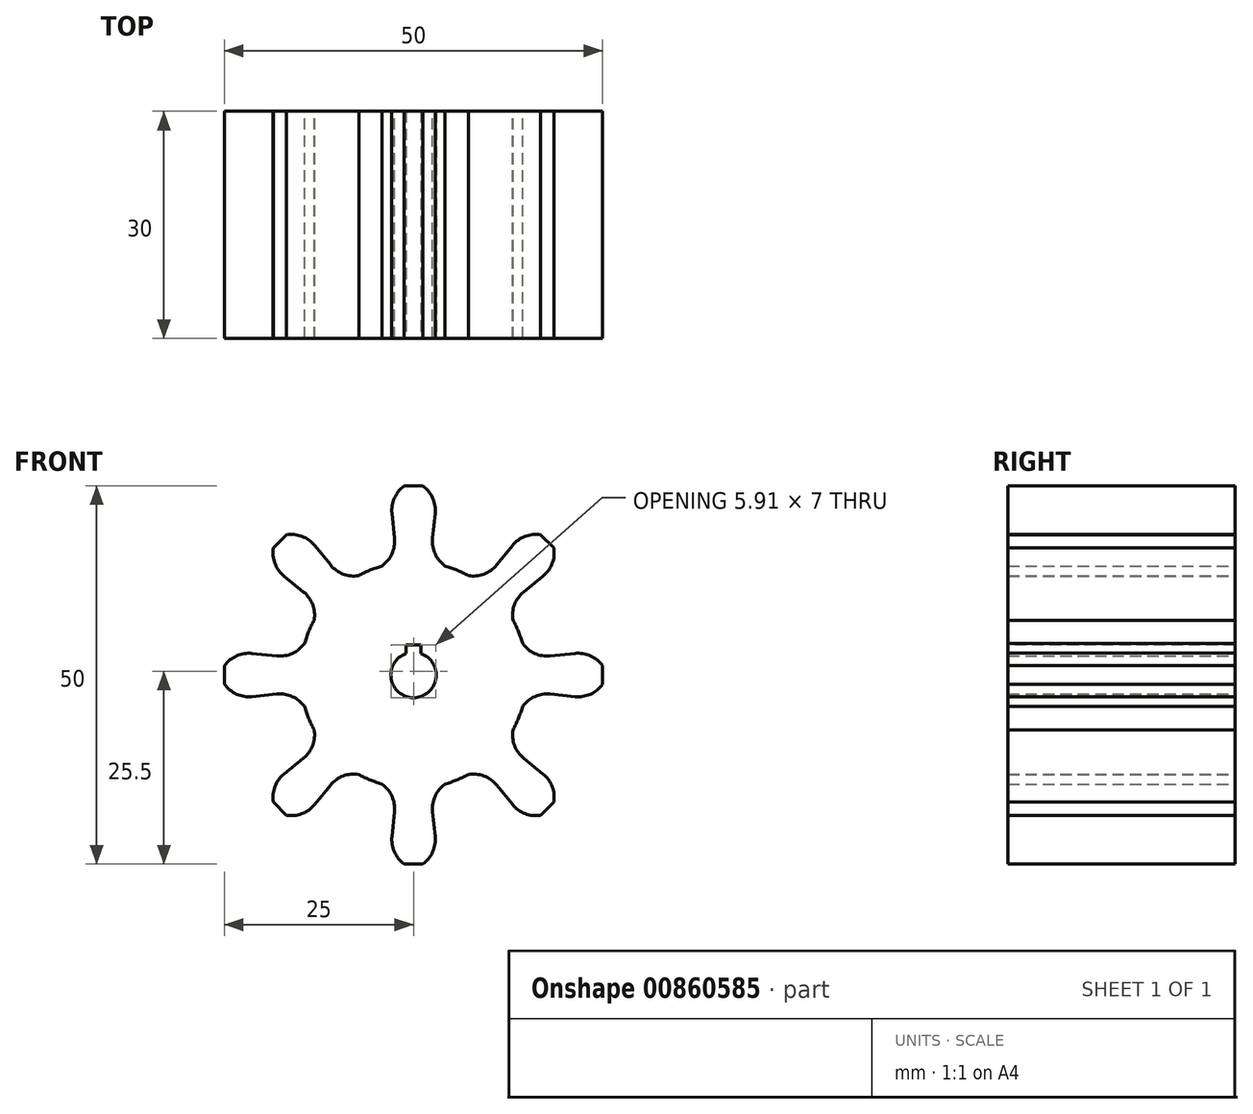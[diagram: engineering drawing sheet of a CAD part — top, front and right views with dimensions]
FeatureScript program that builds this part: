
annotation { "Feature Type Name" : "Feature", "Feature Type Description" : "" }
export const myFeature = defineFeature(function(context is Context, id is Id, definition is map)
    precondition{}
    {
        {
            var Q0;
            Q0=qCreatedBy(makeId("Front.planeOp"),FACE);
            var sketch = newSketch(context, id + "F0", { "sketchPlane" : qUnion([Q0])});
            skArc(sketch, "E0", {"start": v(-13.14, 7.24) * mm, "mid": v(-13.86, 5.74) * mm, "end": v(-14.4, 4.17) * mm});
            skArc(sketch, "E1", {"start": v(-4.17, 14.4) * mm, "mid": v(-2.86, 16.01) * mm, "end": v(-2.53, 18.06) * mm});
            skLineSegment(sketch, "E2", {"start": v(-2.53, 18.06) * mm, "end": v(-2.86, 21.35) * mm});
            skLineSegment(sketch, "E3", {"start": v(-1.22, 25) * mm, "end": v(1.22, 25) * mm});
            skArc(sketch, "E4", {"start": v(-1.22, 25) * mm, "mid": v(-2.53, 23.4) * mm, "end": v(-2.86, 21.35) * mm});
            skArc(sketch, "E5.MirrorCS", {"start": v(1.22, 25) * mm, "mid": v(2.53, 23.4) * mm, "end": v(2.86, 21.35) * mm});
            skLineSegment(sketch, "E6.MirrorCS", {"start": v(2.53, 18.06) * mm, "end": v(2.86, 21.35) * mm});
            skArc(sketch, "E7.MirrorCS", {"start": v(4.17, 14.4) * mm, "mid": v(2.86, 16.01) * mm, "end": v(2.53, 18.06) * mm});
            skLineSegment(sketch, "E8.1.0", {"start": v(-18.54, 16.81) * mm, "end": v(-16.81, 18.54) * mm});
            skArc(sketch, "E8.1.1", {"start": v(-18.54, 16.81) * mm, "mid": v(-18.33, 14.75) * mm, "end": v(-17.12, 13.07) * mm});
            skLineSegment(sketch, "E8.1.2", {"start": v(-14.56, 10.98) * mm, "end": v(-17.12, 13.07) * mm});
            skArc(sketch, "E8.1.3", {"start": v(-13.14, 7.24) * mm, "mid": v(-13.34, 9.3) * mm, "end": v(-14.56, 10.98) * mm});
            skArc(sketch, "E8.1.4", {"start": v(-7.24, 13.14) * mm, "mid": v(-9.3, 13.34) * mm, "end": v(-10.98, 14.56) * mm});
            skLineSegment(sketch, "E8.1.5", {"start": v(-10.98, 14.56) * mm, "end": v(-13.07, 17.12) * mm});
            skArc(sketch, "E8.1.6", {"start": v(-16.81, 18.54) * mm, "mid": v(-14.75, 18.33) * mm, "end": v(-13.07, 17.12) * mm});
            skLineSegment(sketch, "E8.2.0", {"start": v(-25, -1.22) * mm, "end": v(-25, 1.22) * mm});
            skArc(sketch, "E8.2.1", {"start": v(-25, -1.22) * mm, "mid": v(-23.4, -2.53) * mm, "end": v(-21.35, -2.86) * mm});
            skLineSegment(sketch, "E8.2.2", {"start": v(-18.06, -2.53) * mm, "end": v(-21.35, -2.86) * mm});
            skArc(sketch, "E8.2.3", {"start": v(-14.4, -4.17) * mm, "mid": v(-16.01, -2.86) * mm, "end": v(-18.06, -2.53) * mm});
            skArc(sketch, "E8.2.4", {"start": v(-14.4, 4.17) * mm, "mid": v(-16.01, 2.86) * mm, "end": v(-18.06, 2.53) * mm});
            skLineSegment(sketch, "E8.2.5", {"start": v(-18.06, 2.53) * mm, "end": v(-21.35, 2.86) * mm});
            skArc(sketch, "E8.2.6", {"start": v(-25, 1.22) * mm, "mid": v(-23.4, 2.53) * mm, "end": v(-21.35, 2.86) * mm});
            skLineSegment(sketch, "E8.3.0", {"start": v(-16.81, -18.54) * mm, "end": v(-18.54, -16.81) * mm});
            skArc(sketch, "E8.3.1", {"start": v(-16.81, -18.54) * mm, "mid": v(-14.75, -18.33) * mm, "end": v(-13.07, -17.12) * mm});
            skLineSegment(sketch, "E8.3.2", {"start": v(-10.98, -14.56) * mm, "end": v(-13.07, -17.12) * mm});
            skArc(sketch, "E8.3.3", {"start": v(-7.24, -13.14) * mm, "mid": v(-9.3, -13.34) * mm, "end": v(-10.98, -14.56) * mm});
            skArc(sketch, "E8.3.4", {"start": v(-13.14, -7.24) * mm, "mid": v(-13.34, -9.3) * mm, "end": v(-14.56, -10.98) * mm});
            skLineSegment(sketch, "E8.3.5", {"start": v(-14.56, -10.98) * mm, "end": v(-17.12, -13.07) * mm});
            skArc(sketch, "E8.3.6", {"start": v(-18.54, -16.81) * mm, "mid": v(-18.33, -14.75) * mm, "end": v(-17.12, -13.07) * mm});
            skLineSegment(sketch, "E8.4.0", {"start": v(1.22, -25) * mm, "end": v(-1.22, -25) * mm});
            skArc(sketch, "E8.4.1", {"start": v(1.22, -25) * mm, "mid": v(2.53, -23.4) * mm, "end": v(2.86, -21.35) * mm});
            skLineSegment(sketch, "E8.4.2", {"start": v(2.53, -18.06) * mm, "end": v(2.86, -21.35) * mm});
            skArc(sketch, "E8.4.3", {"start": v(4.17, -14.4) * mm, "mid": v(2.86, -16.01) * mm, "end": v(2.53, -18.06) * mm});
            skArc(sketch, "E8.4.4", {"start": v(-4.17, -14.4) * mm, "mid": v(-2.86, -16.01) * mm, "end": v(-2.53, -18.06) * mm});
            skLineSegment(sketch, "E8.4.5", {"start": v(-2.53, -18.06) * mm, "end": v(-2.86, -21.35) * mm});
            skArc(sketch, "E8.4.6", {"start": v(-1.22, -25) * mm, "mid": v(-2.53, -23.4) * mm, "end": v(-2.86, -21.35) * mm});
            skLineSegment(sketch, "E8.5.0", {"start": v(18.54, -16.81) * mm, "end": v(16.81, -18.54) * mm});
            skArc(sketch, "E8.5.1", {"start": v(18.54, -16.81) * mm, "mid": v(18.33, -14.75) * mm, "end": v(17.12, -13.07) * mm});
            skLineSegment(sketch, "E8.5.2", {"start": v(14.56, -10.98) * mm, "end": v(17.12, -13.07) * mm});
            skArc(sketch, "E8.5.3", {"start": v(13.14, -7.24) * mm, "mid": v(13.34, -9.3) * mm, "end": v(14.56, -10.98) * mm});
            skArc(sketch, "E8.5.4", {"start": v(7.24, -13.14) * mm, "mid": v(9.3, -13.34) * mm, "end": v(10.98, -14.56) * mm});
            skLineSegment(sketch, "E8.5.5", {"start": v(10.98, -14.56) * mm, "end": v(13.07, -17.12) * mm});
            skArc(sketch, "E8.5.6", {"start": v(16.81, -18.54) * mm, "mid": v(14.75, -18.33) * mm, "end": v(13.07, -17.12) * mm});
            skLineSegment(sketch, "E8.6.0", {"start": v(25, 1.22) * mm, "end": v(25, -1.22) * mm});
            skArc(sketch, "E8.6.1", {"start": v(25, 1.22) * mm, "mid": v(23.4, 2.53) * mm, "end": v(21.35, 2.86) * mm});
            skLineSegment(sketch, "E8.6.2", {"start": v(18.06, 2.53) * mm, "end": v(21.35, 2.86) * mm});
            skArc(sketch, "E8.6.3", {"start": v(14.4, 4.17) * mm, "mid": v(16.01, 2.86) * mm, "end": v(18.06, 2.53) * mm});
            skArc(sketch, "E8.6.4", {"start": v(14.4, -4.17) * mm, "mid": v(16.01, -2.86) * mm, "end": v(18.06, -2.53) * mm});
            skLineSegment(sketch, "E8.6.5", {"start": v(18.06, -2.53) * mm, "end": v(21.35, -2.86) * mm});
            skArc(sketch, "E8.6.6", {"start": v(25, -1.22) * mm, "mid": v(23.4, -2.53) * mm, "end": v(21.35, -2.86) * mm});
            skLineSegment(sketch, "E8.7.0", {"start": v(16.81, 18.54) * mm, "end": v(18.54, 16.81) * mm});
            skArc(sketch, "E8.7.1", {"start": v(16.81, 18.54) * mm, "mid": v(14.75, 18.33) * mm, "end": v(13.07, 17.12) * mm});
            skLineSegment(sketch, "E8.7.2", {"start": v(10.98, 14.56) * mm, "end": v(13.07, 17.12) * mm});
            skArc(sketch, "E8.7.3", {"start": v(7.24, 13.14) * mm, "mid": v(9.3, 13.34) * mm, "end": v(10.98, 14.56) * mm});
            skArc(sketch, "E8.7.4", {"start": v(13.14, 7.24) * mm, "mid": v(13.34, 9.3) * mm, "end": v(14.56, 10.98) * mm});
            skLineSegment(sketch, "E8.7.5", {"start": v(14.56, 10.98) * mm, "end": v(17.12, 13.07) * mm});
            skArc(sketch, "E8.7.6", {"start": v(18.54, 16.81) * mm, "mid": v(18.33, 14.75) * mm, "end": v(17.12, 13.07) * mm});
            skArc(sketch, "E9.trimOffspring", {"start": v(-4.17, 14.4) * mm, "mid": v(-5.74, 13.86) * mm, "end": v(-7.24, 13.14) * mm});
            skArc(sketch, "E10.trimOffspring", {"start": v(7.24, 13.14) * mm, "mid": v(5.74, 13.86) * mm, "end": v(4.17, 14.4) * mm});
            skArc(sketch, "E11.trimOffspring", {"start": v(14.4, 4.17) * mm, "mid": v(13.86, 5.74) * mm, "end": v(13.14, 7.24) * mm});
            skArc(sketch, "E12.trimOffspring", {"start": v(13.14, -7.24) * mm, "mid": v(13.86, -5.74) * mm, "end": v(14.4, -4.17) * mm});
            skArc(sketch, "E13.trimOffspring", {"start": v(4.17, -14.4) * mm, "mid": v(5.74, -13.86) * mm, "end": v(7.24, -13.14) * mm});
            skArc(sketch, "E14.trimOffspring", {"start": v(-7.24, -13.14) * mm, "mid": v(-5.74, -13.86) * mm, "end": v(-4.17, -14.4) * mm});
            skArc(sketch, "E15.trimOffspring", {"start": v(-14.4, -4.17) * mm, "mid": v(-13.86, -5.74) * mm, "end": v(-13.14, -7.24) * mm});
            skSolve(sketch);
        }
        {
            var Q0;
            Q0 = qSketchRegion(id + "F0", true);
            extrude(context, id + "F1", {"entities" : qUnion([Q0]), "depth" : 30 * mm, "offsetDistance" : 25 * mm});
        }
        {
            var Q0;
            Q0=makeQuery(id+"F1.opExtrude","CAP_FACE",FACE,{"disambiguationData":[OSD([sQuery(id+"F0.wireOp",EDGE,"E0"),sQuery(id+"F0.wireOp",EDGE,"E1"),sQuery(id+"F0.wireOp",EDGE,"E2"),sQuery(id+"F0.wireOp",EDGE,"E3"),sQuery(id+"F0.wireOp",EDGE,"E4"),sQuery(id+"F0.wireOp",EDGE,"E5.MirrorCS"),sQuery(id+"F0.wireOp",EDGE,"E6.MirrorCS"),sQuery(id+"F0.wireOp",EDGE,"E7.MirrorCS"),sQuery(id+"F0.wireOp",EDGE,"E8.1.0"),sQuery(id+"F0.wireOp",EDGE,"E8.1.1"),sQuery(id+"F0.wireOp",EDGE,"E8.1.2"),sQuery(id+"F0.wireOp",EDGE,"E8.1.3"),sQuery(id+"F0.wireOp",EDGE,"E8.1.4"),sQuery(id+"F0.wireOp",EDGE,"E8.1.5"),sQuery(id+"F0.wireOp",EDGE,"E8.1.6"),sQuery(id+"F0.wireOp",EDGE,"E8.2.0"),sQuery(id+"F0.wireOp",EDGE,"E8.2.1"),sQuery(id+"F0.wireOp",EDGE,"E8.2.2"),sQuery(id+"F0.wireOp",EDGE,"E8.2.3"),sQuery(id+"F0.wireOp",EDGE,"E8.2.4"),sQuery(id+"F0.wireOp",EDGE,"E8.2.5"),sQuery(id+"F0.wireOp",EDGE,"E8.2.6"),sQuery(id+"F0.wireOp",EDGE,"E8.3.0"),sQuery(id+"F0.wireOp",EDGE,"E8.3.1"),sQuery(id+"F0.wireOp",EDGE,"E8.3.2"),sQuery(id+"F0.wireOp",EDGE,"E8.3.3"),sQuery(id+"F0.wireOp",EDGE,"E8.3.4"),sQuery(id+"F0.wireOp",EDGE,"E8.3.5"),sQuery(id+"F0.wireOp",EDGE,"E8.3.6"),sQuery(id+"F0.wireOp",EDGE,"E8.4.0"),sQuery(id+"F0.wireOp",EDGE,"E8.4.1"),sQuery(id+"F0.wireOp",EDGE,"E8.4.2"),sQuery(id+"F0.wireOp",EDGE,"E8.4.3"),sQuery(id+"F0.wireOp",EDGE,"E8.4.4"),sQuery(id+"F0.wireOp",EDGE,"E8.4.5"),sQuery(id+"F0.wireOp",EDGE,"E8.4.6"),sQuery(id+"F0.wireOp",EDGE,"E8.5.0"),sQuery(id+"F0.wireOp",EDGE,"E8.5.1"),sQuery(id+"F0.wireOp",EDGE,"E8.5.2"),sQuery(id+"F0.wireOp",EDGE,"E8.5.3"),sQuery(id+"F0.wireOp",EDGE,"E8.5.4"),sQuery(id+"F0.wireOp",EDGE,"E8.5.5"),sQuery(id+"F0.wireOp",EDGE,"E8.5.6"),sQuery(id+"F0.wireOp",EDGE,"E8.6.0"),sQuery(id+"F0.wireOp",EDGE,"E8.6.1"),sQuery(id+"F0.wireOp",EDGE,"E8.6.2"),sQuery(id+"F0.wireOp",EDGE,"E8.6.3"),sQuery(id+"F0.wireOp",EDGE,"E8.6.4"),sQuery(id+"F0.wireOp",EDGE,"E8.6.5"),sQuery(id+"F0.wireOp",EDGE,"E8.6.6"),sQuery(id+"F0.wireOp",EDGE,"E8.7.0"),sQuery(id+"F0.wireOp",EDGE,"E8.7.1"),sQuery(id+"F0.wireOp",EDGE,"E8.7.2"),sQuery(id+"F0.wireOp",EDGE,"E8.7.3"),sQuery(id+"F0.wireOp",EDGE,"E8.7.4"),sQuery(id+"F0.wireOp",EDGE,"E8.7.5"),sQuery(id+"F0.wireOp",EDGE,"E8.7.6"),sQuery(id+"F0.wireOp",EDGE,"E9.trimOffspring"),sQuery(id+"F0.wireOp",EDGE,"E10.trimOffspring"),sQuery(id+"F0.wireOp",EDGE,"E11.trimOffspring"),sQuery(id+"F0.wireOp",EDGE,"E12.trimOffspring"),sQuery(id+"F0.wireOp",EDGE,"E13.trimOffspring"),sQuery(id+"F0.wireOp",EDGE,"E14.trimOffspring"),sQuery(id+"F0.wireOp",EDGE,"E15.trimOffspring")])],"isStart":false});
            var sketch = newSketch(context, id + "F2", { "sketchPlane" : qUnion([Q0])});
            skPoint(sketch, "E16.0.midPoint", {"position": v(2.04, 3.54) * mm});
            skArc(sketch, "E17", {"start": v(-1, 2.83) * mm, "mid": v(0, -3) * mm, "end": v(1, 2.83) * mm});
            skLineSegment(sketch, "E18", {"start": v(-1, 2.83) * mm, "end": v(-1, 4) * mm});
            skLineSegment(sketch, "E19", {"start": v(-1, 4) * mm, "end": v(1, 4) * mm});
            skLineSegment(sketch, "E20", {"start": v(1, 4) * mm, "end": v(1, 2.83) * mm});
            skSolve(sketch);
        }
        {
            var Q0;
            Q0 = qSketchRegion(id + "F2", true);
            extrude(context, id + "F3", {"entities" : qUnion([Q0]), "operationType" : NewBodyOperationType.REMOVE, "endBound" : BoundingType.THROUGH_ALL, "oppositeDirection" : true, "depth" : 25 * mm, "offsetDistance" : 25 * mm});
        }
    });
